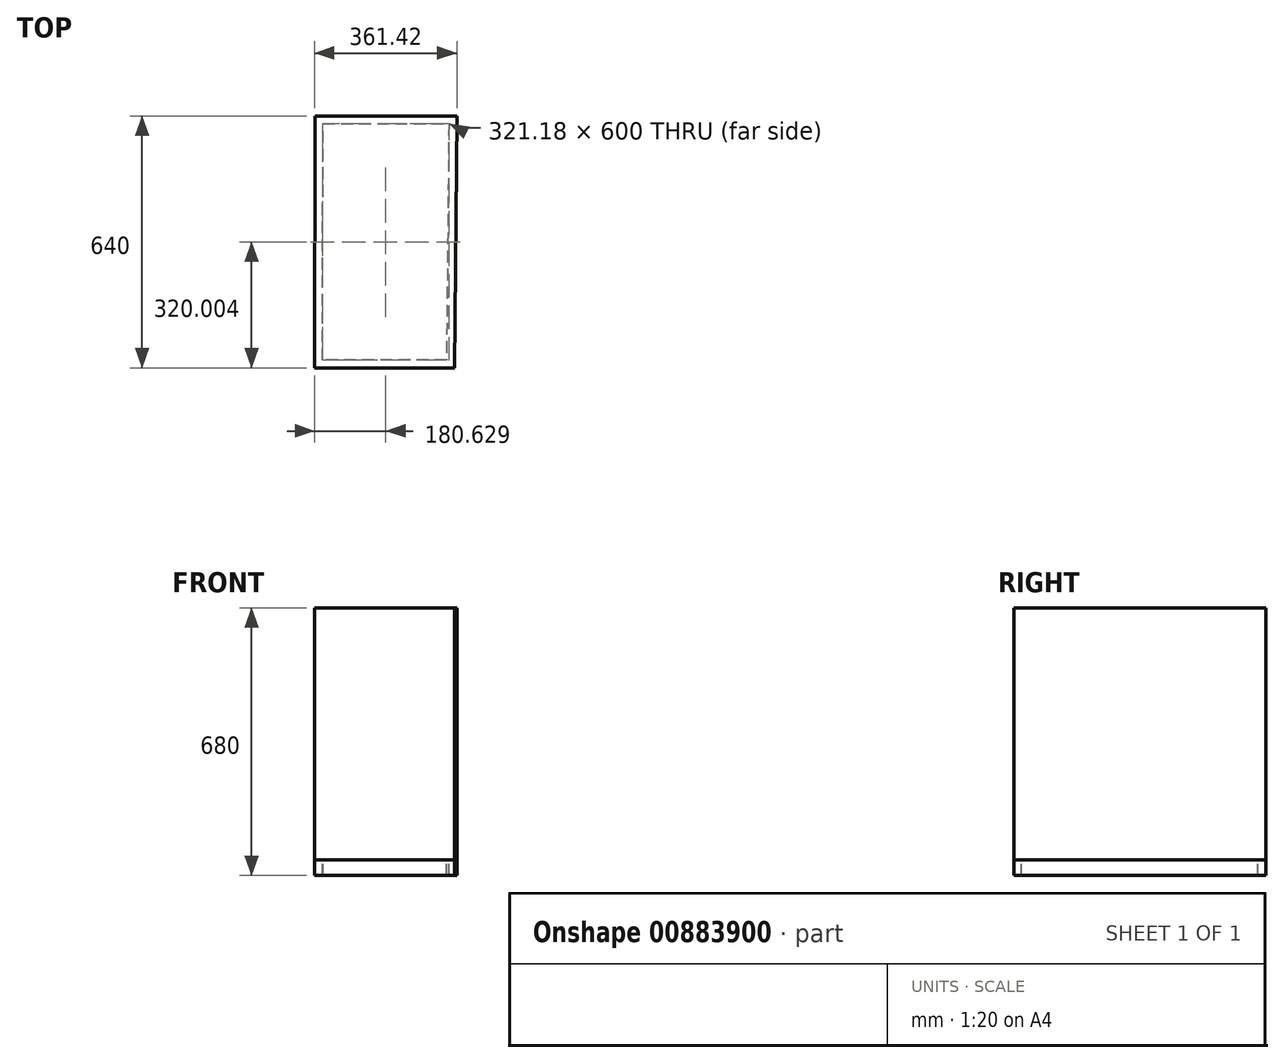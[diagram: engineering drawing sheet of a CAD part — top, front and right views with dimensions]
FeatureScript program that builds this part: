
annotation { "Feature Type Name" : "Feature", "Feature Type Description" : "" }
export const myFeature = defineFeature(function(context is Context, id is Id, definition is map)
    precondition{}
    {
        {
            var Q0;
            Q0=qCreatedBy(makeId("Top.planeOp"),FACE);
            var sketch = newSketch(context, id + "F0", { "sketchPlane" : qUnion([Q0])});
            skLineSegment(sketch, "E0", {"start": v(-233.75, 288.88) * mm, "end": v(126.25, 288.88) * mm});
            skLineSegment(sketch, "E1", {"start": v(126.25, 288.88) * mm, "end": v(119.83, -351.09) * mm});
            skLineSegment(sketch, "E2", {"start": v(119.83, -351.09) * mm, "end": v(-235.17, -351.12) * mm});
            skLineSegment(sketch, "E3", {"start": v(-235.17, -351.12) * mm, "end": v(-233.75, 288.88) * mm});
            skLineSegment(sketch, "E4.0", {"start": v(-213.8, 268.88) * mm, "end": v(106.05, 268.88) * mm});
            skLineSegment(sketch, "E4.1", {"start": v(-215.13, -331.11) * mm, "end": v(-213.8, 268.88) * mm});
            skLineSegment(sketch, "E4.2", {"start": v(100.03, -331.09) * mm, "end": v(-215.13, -331.11) * mm});
            skLineSegment(sketch, "E4.3", {"start": v(106.05, 268.88) * mm, "end": v(100.03, -331.09) * mm});
            skSolve(sketch);
        }
        {
            var Q0;
            Q0=makeQuery(id+"F0.imprint","IMPRINT",FACE,{"disambiguationData":[TD([[makeQuery(id+"F0.imprint","IMPRINT",EDGE,{"derivedFrom":sQuery(id+"F0.wireOp",EDGE,"E0")}),-1.0]])]});
            var Q1;
            Q1=makeQuery(id+"F0.imprint","IMPRINT",FACE,{"disambiguationData":[TD([[makeQuery(id+"F0.imprint","IMPRINT",EDGE,{"derivedFrom":sQuery(id+"F0.wireOp",EDGE,"E4.0")}),-1.0]])]});
            extrude(context, id + "F1", {"entities" : qUnion([Q0, Q1]), "depth" : 640 * mm, "offsetDistance" : 25 * mm});
        }
        {
            var Q0;
            Q0=makeQuery(id+"F0.imprint","IMPRINT",FACE,{"disambiguationData":[TD([[makeQuery(id+"F0.imprint","IMPRINT",EDGE,{"derivedFrom":sQuery(id+"F0.wireOp",EDGE,"E0")}),-1.0]])]});
            extrude(context, id + "F2", {"entities" : qUnion([Q0]), "oppositeDirection" : true, "depth" : 40 * mm, "offsetDistance" : 25 * mm});
        }
    });
